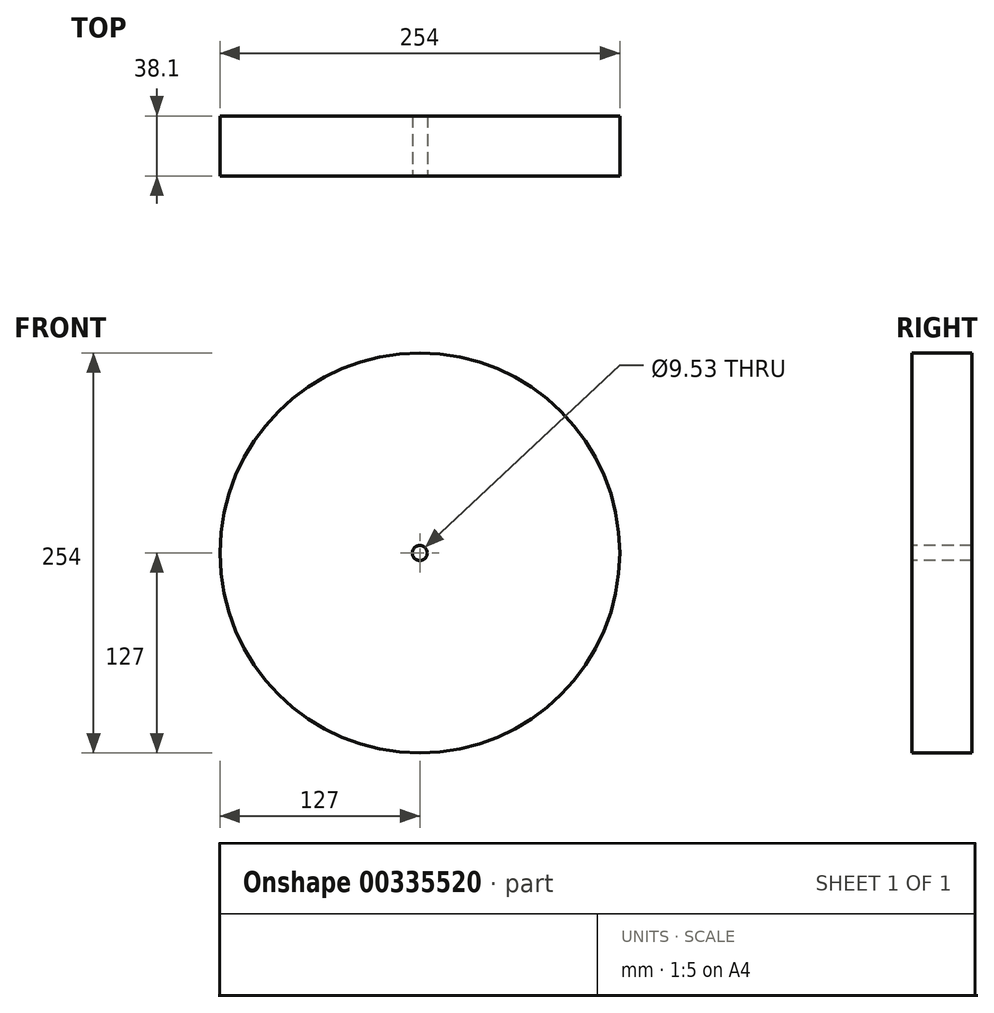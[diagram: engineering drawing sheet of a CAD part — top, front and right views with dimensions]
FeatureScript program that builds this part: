
annotation { "Feature Type Name" : "Feature", "Feature Type Description" : "" }
export const myFeature = defineFeature(function(context is Context, id is Id, definition is map)
    precondition{}
    {
        {
            var Q0;
            Q0=qCreatedBy(makeId("Front.planeOp"),FACE);
            var sketch = newSketch(context, id + "F0", { "sketchPlane" : qUnion([Q0])});
            skCircle(sketch, "E0", {"center": v(0, 0) * mm, "radius": 127 * mm});
            skSolve(sketch);
        }
        {
            var Q0;
            Q0=makeQuery(id+"F0.imprint","IMPRINT",FACE,{"disambiguationData":[TD([[makeQuery(id+"F0.imprint","IMPRINT",EDGE,{"derivedFrom":sQuery(id+"F0.wireOp",EDGE,"E0")}),1.0]])]});
            extrude(context, id + "F1", {"entities" : qUnion([Q0]), "endBound" : BoundingType.SYMMETRIC, "depth" : 38.1 * mm});
        }
        {
            var Q0;
            Q0=makeQuery(id+"F1.opExtrude","CAP_FACE",FACE,{"disambiguationData":[OSD([sQuery(id+"F0.wireOp",EDGE,"E0")])],"isStart":false});
            var sketch = newSketch(context, id + "F2", { "sketchPlane" : qUnion([Q0])});
            skPoint(sketch, "E1", {"position": v(0, 0) * mm});
            skSolve(sketch);
        }
        {
            var Q0;
            Q0=sQuery(id+"F2.wireOp",VERTEX,"E1");
            var Q1;
            Q1=makeQuery(id+"F1.opExtrude","SWEPT_BODY",BODY,{"disambiguationData":[OSD([sQuery(id+"F0.wireOp",EDGE,"E0")])]});
            hole(context, id + "F3", {"style" : HoleStyle.SIMPLE, "endStyle" : HoleEndStyle.THROUGH, "holeDiameter" : 9.52 * mm, "tappedDepth" : 12.7 * mm, "tapClearance" : 3, "locations" : qUnion([Q0]), "scope" : qUnion([Q1])});
        }
    });
